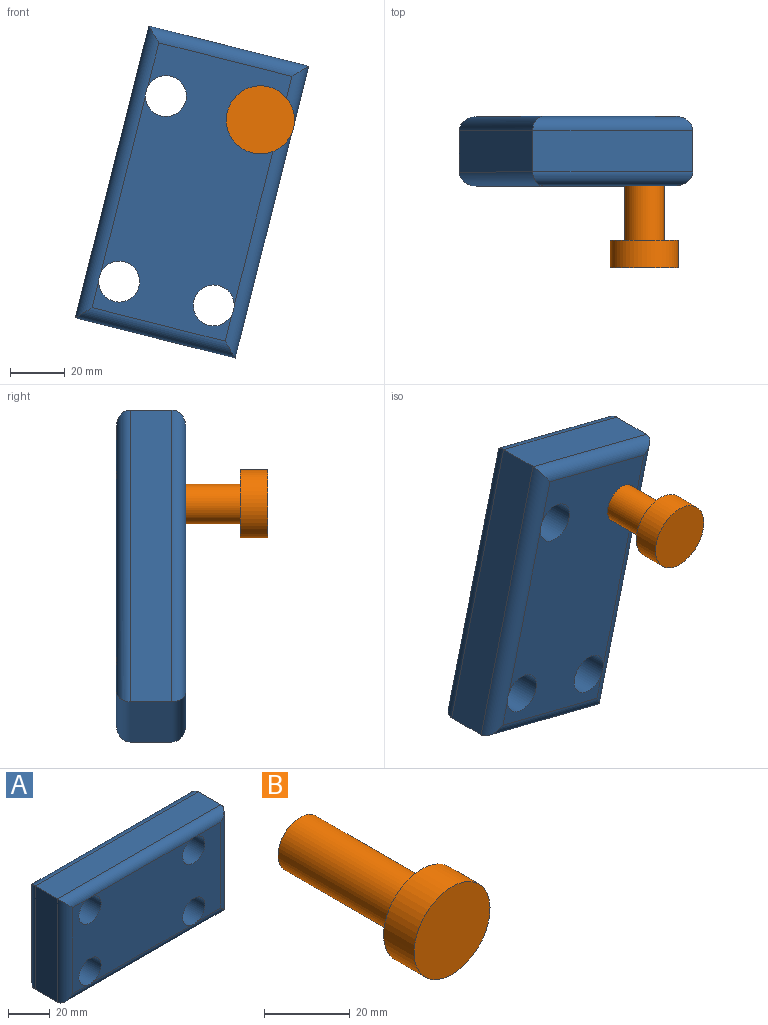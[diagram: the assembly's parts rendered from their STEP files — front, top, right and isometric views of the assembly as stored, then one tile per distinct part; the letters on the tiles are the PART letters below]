
ASSEMBLY  parts=2 mates=3
PART A: 18 faces, bbox 110.3x25.4x60.4 mm
  f0: plane 60.44x15.24mm, normal (1,0,0), area 921.1mm2, adj f1,f6,f11,f15
  f1: plane 110.29x15.24mm, normal (0,0,1), area 1680.9mm2, adj f0,f2,f10,f14
  f2: plane 60.44x15.24mm, normal (-1,0,0), area 921.1mm2, adj f1,f6,f12,f16
  f3: cylinder r=7.5mm len=25.4mm, axis (0,1,0), area 1196.9mm2, adj f8,f9,f13,f17
  f4: cylinder r=7.5mm len=25.4mm, axis (0,1,0), area 1196.9mm2, adj f8,f9,f13,f17
  f5: cylinder r=7.5mm len=25.4mm, axis (0,1,0), area 1196.9mm2, adj f8,f9,f10,f14
  f6: plane 110.29x15.24mm, normal (0,0,-1), area 1680.9mm2, adj f0,f2,f13,f17
  f7: cylinder r=7.5mm len=25.4mm, axis (0,1,0), area 1196.9mm2, adj f8,f9,f10,f14
  f8: plane 100.13x50.28mm, normal (0,-1,0), area 4330.2mm2, adj f3,f4,f5,f7,f14,f15,f16,f17
  f9: plane 100.13x50.28mm, normal (0,1,0), area 4330.2mm2, adj f3,f4,f5,f7,f10,f11,f12,f13
  f10: cylinder r=5.08mm len=110.29mm, axis (-1,0,0), area 849.5mm2, adj f1,f5,f7,f9,f11,f12
  f11: cylinder r=5.08mm len=60.44mm, axis (0,0,1), area 452.8mm2, adj f0,f9,f10,f13
  f12: cylinder r=5.08mm len=60.44mm, axis (0,0,-1), area 452.8mm2, adj f2,f9,f10,f13
  f13: cylinder r=5.08mm len=110.29mm, axis (1,0,0), area 849.5mm2, adj f3,f4,f6,f9,f11,f12
  f14: cylinder r=5.08mm len=110.29mm, axis (1,0,0), area 849.5mm2, adj f1,f5,f7,f8,f15,f16
  f15: cylinder r=5.08mm len=60.44mm, axis (0,0,-1), area 452.8mm2, adj f0,f8,f14,f17
  f16: cylinder r=5.08mm len=60.44mm, axis (0,0,1), area 452.8mm2, adj f2,f8,f14,f17
  f17: cylinder r=5.08mm len=110.29mm, axis (-1,0,0), area 849.5mm2, adj f3,f4,f6,f8,f15,f16
PART B: 5 faces, bbox 25x50x25 mm
  f0: cylinder r=7.25mm len=40mm, axis (0,1,0), area 1822.1mm2, adj f1,f4
  f1: plane 14.5x14.5mm, normal (0,1,0), area 165.1mm2, adj f0
  f2: cylinder r=12.5mm len=25mm, axis (0,1,0), area 785.4mm2, adj f3,f4
  f3: plane 25x25mm, normal (0,-1,0), area 490.9mm2, adj f2
  f4: plane 25x25mm, normal (0,1,0), area 325.7mm2, adj f0,f2
PLACE A rot(axis=(0,-1,0),75.9deg) t=(-97.72,30.01,-5.26)mm
PLACE B t=(79,24.61,-18.29)mm fixed
MATE cylindrical B.f0 <-> A.f3  axis (0,1,0) through (-71.83,4.61,24.39)mm
MATE pin_slot A.f8 <-> B.f0  axis (0,-1,0) through (-64.33,4.61,24.39)mm
MATE slider B.f0 <-> B.f0  axis (0,1,0) through (-71.83,-15.39,24.39)mm
